annotation { "Feature Type Name" : "Feature", "Feature Type Description" : "" }
export const myFeature = defineFeature(function(context is Context, id is Id, definition is map)
    precondition{}
    {
        {
            var Q0;
            Q0=qCreatedBy(makeId("Top.planeOp"),FACE);
            var sketch = newSketch(context, id + "F0", { "sketchPlane" : qUnion([Q0])});
            skLineSegment(sketch, "E0.bottom", {"start": v(-50, 0.93) * mm, "end": v(50, 0.93) * mm});
            skLineSegment(sketch, "E0.top", {"start": v(-50, -1.07) * mm, "end": v(50, -1.07) * mm});
            skLineSegment(sketch, "E0.left", {"start": v(-50, 0.93) * mm, "end": v(-50, -1.07) * mm});
            skLineSegment(sketch, "E0.right", {"start": v(50, 0.93) * mm, "end": v(50, -1.07) * mm});
            skPoint(sketch, "E0.middle", {"position": v(0, 0) * mm});
            skSolve(sketch);
        }
        {
            var Q0;
            Q0=qCreatedBy(makeId("Top.planeOp"),FACE);
            var sketch = newSketch(context, id + "F1", { "sketchPlane" : qUnion([Q0])});
            skText(sketch, "E1", { "text": "ERIKA&RAUL", "fontName": "OpenSans-Regular.ttf"});
            skLineSegment(sketch, "E2", {"start": v(23.2, 11.82) * mm, "end": v(24.43, 14.01) * mm});
            skLineSegment(sketch, "E3", {"start": v(24.43, 14.01) * mm, "end": v(23.23, 14.01) * mm});
            skLineSegment(sketch, "E4", {"start": v(23.23, 14.01) * mm, "end": v(22.06, 11.82) * mm});
            const initialGuessF1  = {"E1": [-0.04383, 0, 1, 0, 0.01057]};
            skSetInitialGuess(sketch, initialGuessF1);
            skSolve(sketch);
        }
        {
            var Q0;
            Q0=qCreatedBy(makeId("Top.planeOp"),FACE);
            var sketch = newSketch(context, id + "F2", { "sketchPlane" : qUnion([Q0])});
            skText(sketch, "E5", { "text": "BOLDOG KARACSONYT", "fontName": "OpenSans-Bold.ttf"});
            const initialGuessF2  = {"E5": [-0.05002, -0.00735, 1, 0, 0.00637]};
            skSetInitialGuess(sketch, initialGuessF2);
            skSolve(sketch);
        }
        {
            var Q0;
            Q0=qCreatedBy(makeId("Top.planeOp"),FACE);
            var sketch = newSketch(context, id + "F3", { "sketchPlane" : qUnion([Q0])});
            skLineSegment(sketch, "E6", {"start": v(-46.28, 1.1) * mm, "end": v(-46.28, 44.03) * mm, "construction": true});
            skLineSegment(sketch, "E7", {"start": v(-43.93, 9.86) * mm, "end": v(-39.73, 9.86) * mm});
            skLineSegment(sketch, "E8", {"start": v(-43.93, 14.1) * mm, "end": v(-41.68, 14.1) * mm});
            skLineSegment(sketch, "E9.MirrorCS", {"start": v(-48.63, 14.1) * mm, "end": v(-50.88, 14.1) * mm});
            skLineSegment(sketch, "E10.MirrorCS", {"start": v(-48.63, 9.86) * mm, "end": v(-52.83, 9.86) * mm});
            skLineSegment(sketch, "E11", {"start": v(-46.28, 0) * mm, "end": v(-45.17, 0) * mm});
            skLineSegment(sketch, "E12", {"start": v(-45.17, 0) * mm, "end": v(-45.17, 4.14) * mm});
            skLineSegment(sketch, "E13", {"start": v(-45.17, 4.14) * mm, "end": v(-37.92, 4.22) * mm});
            skLineSegment(sketch, "E14.MirrorCS", {"start": v(-47.4, 4.14) * mm, "end": v(-54.64, 4.22) * mm});
            skLineSegment(sketch, "E15.MirrorCS", {"start": v(-47.4, 0) * mm, "end": v(-47.4, 4.14) * mm});
            skLineSegment(sketch, "E16.MirrorCS", {"start": v(-46.28, 0) * mm, "end": v(-47.4, 0) * mm});
            skArc(sketch, "E17", {"start": v(-43.93, 9.86) * mm, "mid": v(-41.62, 6.3) * mm, "end": v(-37.92, 4.22) * mm});
            skArc(sketch, "E18", {"start": v(-43.93, 14.1) * mm, "mid": v(-42.35, 11.46) * mm, "end": v(-39.73, 9.86) * mm});
            skArc(sketch, "E19", {"start": v(-46.28, 18.97) * mm, "mid": v(-44.4, 16.13) * mm, "end": v(-41.68, 14.1) * mm});
            skArc(sketch, "E20.MirrorCS", {"start": v(-46.28, 18.97) * mm, "mid": v(-48.16, 16.13) * mm, "end": v(-50.88, 14.1) * mm});
            skArc(sketch, "E21.MirrorCS", {"start": v(-48.63, 14.1) * mm, "mid": v(-50.21, 11.46) * mm, "end": v(-52.83, 9.86) * mm});
            skArc(sketch, "E22.MirrorCS", {"start": v(-48.63, 9.86) * mm, "mid": v(-50.94, 6.3) * mm, "end": v(-54.64, 4.22) * mm});
            skLineSegment(sketch, "E23.MirrorCS", {"start": v(48.63, 14.1) * mm, "end": v(50.88, 14.1) * mm});
            skLineSegment(sketch, "E24.MirrorCS", {"start": v(43.93, 14.1) * mm, "end": v(41.68, 14.1) * mm});
            skLineSegment(sketch, "E25.MirrorCS", {"start": v(46.28, 0) * mm, "end": v(45.17, 0) * mm});
            skLineSegment(sketch, "E26.MirrorCS", {"start": v(46.28, 0) * mm, "end": v(47.4, 0) * mm});
            skLineSegment(sketch, "E27.MirrorCS", {"start": v(47.4, 0) * mm, "end": v(47.4, 4.14) * mm});
            skLineSegment(sketch, "E28.MirrorCS", {"start": v(48.63, 9.86) * mm, "end": v(52.83, 9.86) * mm});
            skLineSegment(sketch, "E29.MirrorCS", {"start": v(43.93, 9.86) * mm, "end": v(39.73, 9.86) * mm});
            skLineSegment(sketch, "E30.MirrorCS", {"start": v(45.17, 0) * mm, "end": v(45.17, 4.14) * mm});
            skLineSegment(sketch, "E31.MirrorCS", {"start": v(45.17, 4.14) * mm, "end": v(37.92, 4.22) * mm});
            skLineSegment(sketch, "E32.MirrorCS", {"start": v(46.28, 1.1) * mm, "end": v(46.28, 44.03) * mm, "construction": true});
            skArc(sketch, "E33.MirrorCS", {"start": v(48.63, 9.86) * mm, "mid": v(50.94, 6.3) * mm, "end": v(54.64, 4.22) * mm});
            skArc(sketch, "E34.MirrorCS", {"start": v(43.93, 9.86) * mm, "mid": v(41.62, 6.3) * mm, "end": v(37.92, 4.22) * mm});
            skArc(sketch, "E35.MirrorCS", {"start": v(46.28, 18.97) * mm, "mid": v(48.16, 16.13) * mm, "end": v(50.88, 14.1) * mm});
            skArc(sketch, "E36.MirrorCS", {"start": v(48.63, 14.1) * mm, "mid": v(50.21, 11.46) * mm, "end": v(52.83, 9.86) * mm});
            skLineSegment(sketch, "E37.MirrorCS", {"start": v(47.4, 4.14) * mm, "end": v(54.64, 4.22) * mm});
            skArc(sketch, "E38.MirrorCS", {"start": v(46.28, 18.97) * mm, "mid": v(44.4, 16.13) * mm, "end": v(41.68, 14.1) * mm});
            skArc(sketch, "E39.MirrorCS", {"start": v(43.93, 14.1) * mm, "mid": v(42.35, 11.46) * mm, "end": v(39.73, 9.86) * mm});
            skSolve(sketch);
        }
        {
            var Q0;
            Q0=makeQuery(id+"F0.imprint","IMPRINT",FACE,{"disambiguationData":[TD([[makeQuery(id+"F0.imprint","IMPRINT",EDGE,{"derivedFrom":sQuery(id+"F0.wireOp",EDGE,"E0.bottom")}),-1.0]])]});
            extrude(context, id + "F4", {"entities" : qUnion([Q0]), "oppositeDirection" : true, "depth" : 5 * mm});
        }
        {
            var Q0;
            Q0=makeQuery(id+"F3.imprint","IMPRINT",FACE,{"disambiguationData":[TD([[makeQuery(id+"F3.imprint","IMPRINT",EDGE,{"derivedFrom":sQuery(id+"F3.wireOp",EDGE,"99bd6abd-2973-4c87-b3fa-064b87685f2f16.MirrorCS")}),1.0]])]});
            var Q1;
            Q1=makeQuery(id+"F3.imprint","IMPRINT",FACE,{"disambiguationData":[TD([[makeQuery(id+"F3.imprint","IMPRINT",EDGE,{"derivedFrom":sQuery(id+"F3.wireOp",EDGE,"E7")}),1.0]])]});
            var Q2;
            Q2 = qSketchRegion(id + "F1", true);
            var Q3;
            Q3=makeQuery(id+"F3.imprint","IMPRINT",FACE,{"disambiguationData":[TD([[makeQuery(id+"F3.imprint","IMPRINT",EDGE,{"derivedFrom":sQuery(id+"F3.wireOp",EDGE,"E24.MirrorCS")}),-1.0]])]});
            extrude(context, id + "F5", {"entities" : qUnion([Q0, Q1, Q2, Q3]), "operationType" : NewBodyOperationType.ADD, "oppositeDirection" : true, "depth" : 5 * mm});
        }
        {
            var Q0;
            Q0 = qSketchRegion(id + "F2", true);
            extrude(context, id + "F6", {"entities" : qUnion([Q0]), "oppositeDirection" : true, "depth" : 5 * mm});
        }
    });